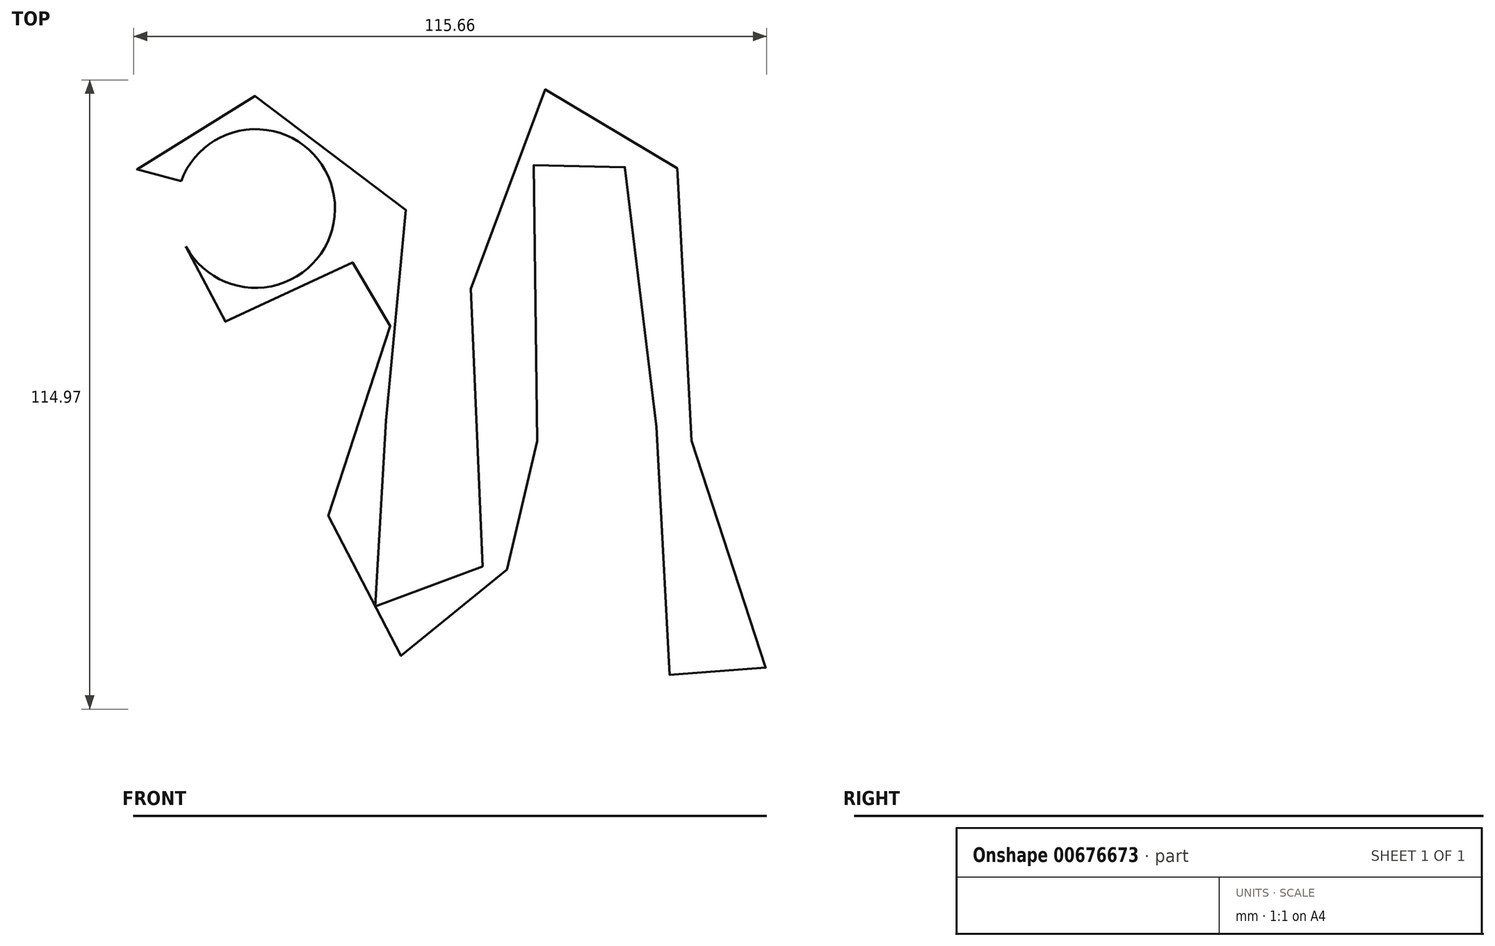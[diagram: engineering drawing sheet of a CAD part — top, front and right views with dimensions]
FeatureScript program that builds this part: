
annotation { "Feature Type Name" : "Feature", "Feature Type Description" : "" }
export const myFeature = defineFeature(function(context is Context, id is Id, definition is map)
    precondition{}
    {
        {
            var Q0;
            Q0=qCreatedBy(makeId("Top.planeOp"),FACE);
            var sketch = newSketch(context, id + "F0", { "sketchPlane" : qUnion([Q0])});
            skCircle(sketch, "E0", {"center": v(-5, -5) * mm, "radius": 14.5 * mm});
            skFitSpline(sketch, "E1", {"points": [v(-18.6, 0) * mm, v(-24.42, -6.71) * mm, v(-27.27, 0) * mm, v(-19.85, 8.7) * mm, v(-2.43, 15.56) * mm, v(21.85, -3.86) * mm, v(20.42, -39.55) * mm, v(13.28, -71.82) * mm, v(28.99, -83.24) * mm, v(37.27, -56.97) * mm, v(36.7, 3.86) * mm, v(56.12, 18.42) * mm, v(72.68, 0) * mm, v(76.96, -62.11) * mm, v(87.81, -92.95) * mm, v(74.68, -95.24) * mm, v(68.4, -65.54) * mm, v(64.11, -2.71) * mm, v(54.97, 11.28) * mm, v(44.4, -2.14) * mm, v(46.4, -56.97) * mm, v(43.26, -61.54) * mm, v(36.41, -83.82) * mm, v(20.7, -86.39) * mm, v(7.85, -69.25) * mm, v(15.85, -38.98) * mm, v(20.13, -16.7) * mm, v(16.7, -12.42) * mm, v(7.85, -19.85) * mm, v(-7.57, -26.42) * mm, v(-23.56, -15.56) * mm, v(-17.73, -11.94) * mm], "startDerivative": vector(-295.68, -525.32) * mm, "endDerivative": vector(498.85, 140.15) * mm});
            skSolve(sketch);
        }
        {
            var Q0;
            {var subQ0=sQuery(id+"F0.wireOp",EDGE,"E1");Q0=makeQuery(id+"F0.imprint","IMPRINT",FACE,{"disambiguationData":[TD([[makeQuery(id+"F0.imprint","IMPRINT",EDGE,{"derivedFrom":subQ0}),-1.0]])]});}
            extrude(context, id + "F1", {"entities" : qUnion([Q0]), "depth" : 1 / 406.4 * mm, "offsetDistance" : 25.4 * mm});
        }
    });
